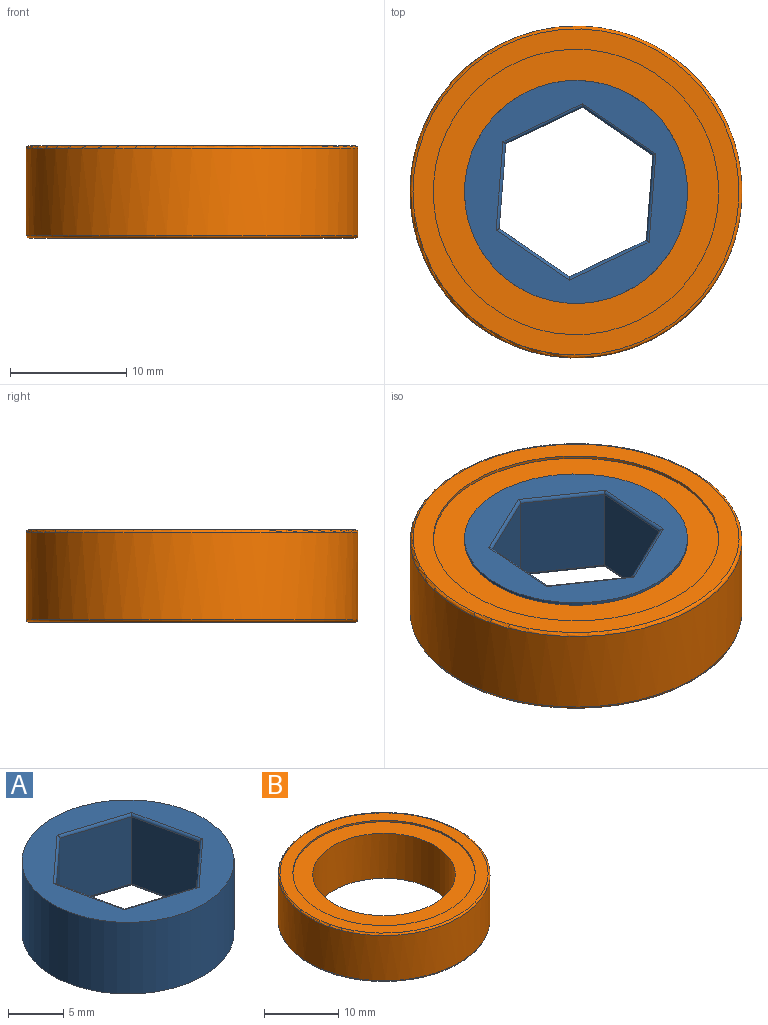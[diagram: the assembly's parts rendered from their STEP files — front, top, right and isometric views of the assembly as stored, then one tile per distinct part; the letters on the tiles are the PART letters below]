
ASSEMBLY  parts=2 mates=1
PART A: 21 faces, bbox 19.2x19.2x7.9 mm
  f0: plane 7.43x5.41mm, normal (-0.67,0.74,0), area 54.5mm2, adj f1,f5,f12,f18
  f1: plane 7.43x6.99mm, normal (0.3,0.95,0), area 54.5mm2, adj f0,f2,f10,f16
  f2: plane 7.43x7.16mm, normal (0.98,0.22,0), area 54.5mm2, adj f1,f3,f9,f15
  f3: plane 7.43x5.41mm, normal (0.67,-0.74,0), area 54.5mm2, adj f2,f4,f11,f17
  f4: plane 7.43x6.99mm, normal (-0.3,-0.95,0), area 54.5mm2, adj f3,f5,f13,f19
  f5: plane 7.43x7.16mm, normal (-0.98,-0.22,0), area 54.5mm2, adj f0,f4,f14,f20
  f6: cylinder r=9.6mm len=19.2mm, axis (0,0,-1), area 478.9mm2, adj f7,f8
  f7: plane 19.2x19.2mm, normal (0,0,1), area 138.6mm2, adj f6,f15,f16,f17,f18,f19,f20
  f8: plane 19.2x19.2mm, normal (0,0,-1), area 138.6mm2, adj f6,f9,f10,f11,f12,f13,f14
  f9: cylinder r=0.25mm len=7.5mm, axis (-0.22,0.98,0), area 3mm2, adj f2,f8,f10,f11
  f10: cylinder r=0.25mm len=7.35mm, axis (-0.95,0.3,0), area 3mm2, adj f1,f8,f9,f12
  f11: cylinder r=0.25mm len=5.8mm, axis (0.74,0.67,0), area 3mm2, adj f3,f8,f9,f13
  f12: cylinder r=0.25mm len=5.8mm, axis (-0.74,-0.67,0), area 3mm2, adj f0,f8,f10,f14
  f13: cylinder r=0.25mm len=7.35mm, axis (0.95,-0.3,0), area 3mm2, adj f4,f8,f11,f14
  f14: cylinder r=0.25mm len=7.5mm, axis (0.22,-0.98,0), area 3mm2, adj f5,f8,f12,f13
  f15: cylinder r=0.25mm len=7.5mm, axis (0.22,-0.98,0), area 3mm2, adj f2,f7,f16,f17
  f16: cylinder r=0.25mm len=7.35mm, axis (0.95,-0.3,0), area 3mm2, adj f1,f7,f15,f18
  f17: cylinder r=0.25mm len=5.8mm, axis (-0.74,-0.67,0), area 3mm2, adj f3,f7,f15,f19
  f18: cylinder r=0.25mm len=5.8mm, axis (0.74,0.67,0), area 3mm2, adj f0,f7,f16,f20
  f19: cylinder r=0.25mm len=7.35mm, axis (-0.95,0.3,0), area 3mm2, adj f4,f7,f17,f20
  f20: cylinder r=0.25mm len=7.5mm, axis (-0.22,0.98,0), area 3mm2, adj f5,f7,f18,f19
PART B: 10 faces, bbox 30.9x30.9x7.9 mm
  f0: torus R=14.04mm, axis (0,0,-1), area 35mm2, adj f1,f5
  f1: plane 28.08x28.08mm, normal (0,0,1), area 144.7mm2, adj f0,f2
  f2: cylinder r=12.29mm len=24.58mm, axis (0,0,-1), area 19.3mm2, adj f1,f3
  f3: plane 24.58x24.58mm, normal (0,0,1), area 184.7mm2, adj f2,f9
  f4: torus R=14.04mm, axis (0,0,1), area 35mm2, adj f5,f6
  f5: cylinder r=14.29mm len=28.58mm, axis (0,0,-1), area 667.7mm2, adj f0,f4
  f6: plane 28.08x28.08mm, normal (0,0,-1), area 144.7mm2, adj f4,f7
  f7: cylinder r=12.29mm len=24.58mm, axis (0,0,-1), area 19.3mm2, adj f6,f8
  f8: plane 24.58x24.58mm, normal (0,0,-1), area 184.7mm2, adj f7,f9
  f9: cylinder r=9.6mm len=19.2mm, axis (0,0,1), area 448.7mm2, adj f3,f8
PLACE A rot(axis=(0,0,-1),16.9deg) t=(-506.1,-132.4,-78.22)mm
PLACE B t=(-73.57,-88.33,466.91)mm fixed
MATE revolute A.f6 <-> B.f0  axis (0,0,-1) through (-506.1,-132.4,-74.25)mm
